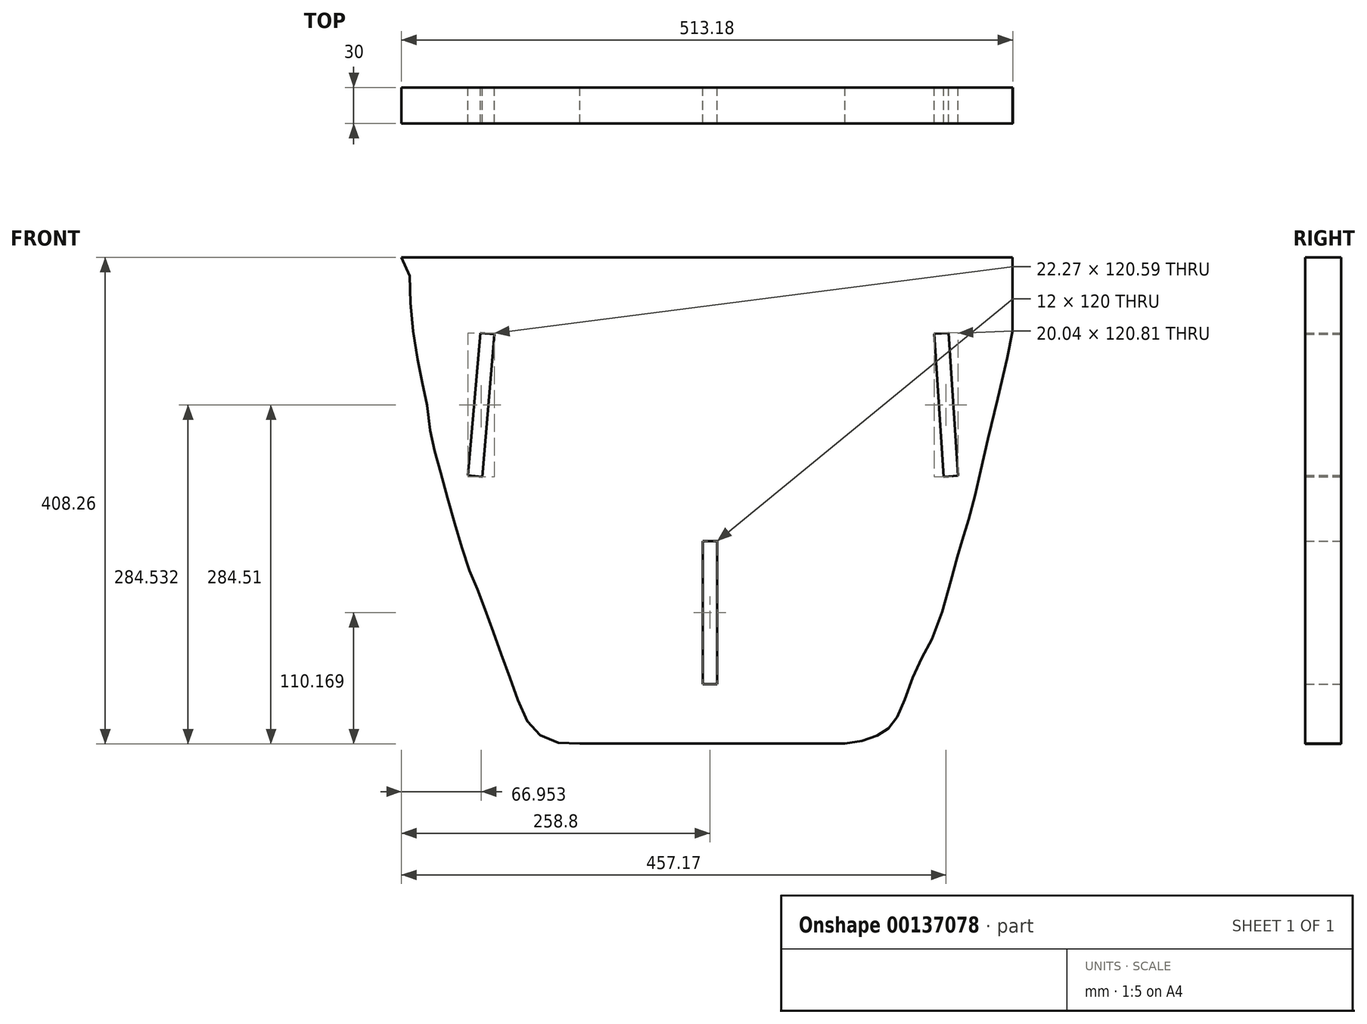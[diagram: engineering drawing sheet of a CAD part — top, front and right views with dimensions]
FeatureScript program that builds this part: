
annotation { "Feature Type Name" : "Feature", "Feature Type Description" : "" }
export const myFeature = defineFeature(function(context is Context, id is Id, definition is map)
    precondition{}
    {
        {
            var Q0;
            Q0=qCreatedBy(makeId("Front.planeOp"),FACE);
            var sketch = newSketch(context, id + "F0", { "sketchPlane" : qUnion([Q0])});
            skLineSegment(sketch, "E0", {"start": v(371.95, 251.63) * mm, "end": v(380.02, 131.63) * mm});
            skLineSegment(sketch, "E1", {"start": v(371.95, 251.63) * mm, "end": v(359.98, 250.83) * mm});
            skLineSegment(sketch, "E2", {"start": v(380.02, 131.63) * mm, "end": v(368.05, 130.83) * mm});
            skLineSegment(sketch, "E3", {"start": v(359.98, 250.83) * mm, "end": v(368.05, 130.83) * mm});
            skLineSegment(sketch, "E4", {"start": v(-21.04, 251.5) * mm, "end": v(-31.35, 131.95) * mm});
            skLineSegment(sketch, "E5", {"start": v(-21.04, 251.5) * mm, "end": v(-9.08, 250.47) * mm});
            skLineSegment(sketch, "E6", {"start": v(-31.35, 131.95) * mm, "end": v(-19.4, 130.92) * mm});
            skLineSegment(sketch, "E7", {"start": v(-9.08, 250.47) * mm, "end": v(-19.4, 130.92) * mm});
            skLineSegment(sketch, "E8", {"start": v(171.63, 76.87) * mm, "end": v(177.63, 76.87) * mm});
            skLineSegment(sketch, "E9", {"start": v(171.63, -43.13) * mm, "end": v(177.63, -43.13) * mm});
            skLineSegment(sketch, "E10", {"start": v(177.63, 76.87) * mm, "end": v(177.63, -43.13) * mm});
            skLineSegment(sketch, "E11", {"start": v(171.63, 76.87) * mm, "end": v(165.63, 76.87) * mm});
            skLineSegment(sketch, "E12", {"start": v(171.63, -43.13) * mm, "end": v(165.63, -43.13) * mm});
            skLineSegment(sketch, "E13", {"start": v(165.63, 76.87) * mm, "end": v(165.63, -43.13) * mm});
            skLineSegment(sketch, "E14", {"start": v(425.7, 314.96) * mm, "end": v(-87.17, 314.96) * mm});
            skLineSegment(sketch, "E15", {"start": v(285.12, -92.86) * mm, "end": v(62.42, -92.86) * mm});
            skFitSpline(sketch, "E16", {"points": [v(425.7, 314.96) * mm, v(425.7, 288.47) * mm, v(425.7, 261.81) * mm, v(425.7, 252.12) * mm, v(405.52, 163.66) * mm, v(393.4, 111.56) * mm, v(383.71, 77.63) * mm, v(377.65, 57.04) * mm, v(360.7, 0) * mm, v(346.15, -27.78) * mm, v(334.03, -59.29) * mm, v(325.55, -76.25) * mm, v(317.07, -83.52) * mm, v(303.74, -89.58) * mm, v(285.12, -92.86) * mm], "startDerivative": vector(2.08, -370.27) * mm, "endDerivative": vector(-337.13, -41.06) * mm});
            skFitSpline(sketch, "E17", {"points": [v(62.42, -92.86) * mm, v(46.86, -92.86) * mm, v(34.68, -88.7) * mm, v(24.08, -82.27) * mm, v(17, -71.67) * mm, v(9.61, -54.63) * mm, v(3.5, -37.28) * mm, v(-3.56, -17.67) * mm, v(-10, 0) * mm, v(-16.42, 18) * mm, v(-22.19, 32.86) * mm, v(-26.96, 45.57) * mm, v(-32.91, 59.08) * mm, v(-38.99, 80.78) * mm, v(-45.1, 99.77) * mm, v(-51.2, 123.52) * mm, v(-56.62, 142.51) * mm, v(-60.7, 157.44) * mm, v(-63.4, 172.36) * mm, v(-66.12, 193.4) * mm, v(-70.2, 211.03) * mm, v(-73.58, 228.67) * mm, v(-77.65, 255.13) * mm, v(-79.69, 281.58) * mm, v(-81.05, 303.3) * mm, v(-87.17, 314.96) * mm], "startDerivative": vector(-434.04, -31.01) * mm, "endDerivative": vector(-213.88, 307.85) * mm});
            skSolve(sketch);
        }
        {
            var Q0;
            Q0=makeQuery(id+"F0.imprint","IMPRINT",FACE,{"disambiguationData":[TD([[makeQuery(id+"F0.imprint","IMPRINT",EDGE,{"derivedFrom":sQuery(id+"F0.wireOp",EDGE,"E0")}),1.0]])]});
            var Q1;
            Q1=makeQuery(id+"F0.imprint","IMPRINT",FACE,{"disambiguationData":[TD([[makeQuery(id+"F0.imprint","IMPRINT",EDGE,{"derivedFrom":sQuery(id+"F0.wireOp",EDGE,"LRyQlrmy-n5ZQ-a9FJ-InVH-gw48jRSE0Qn0")}),1.0]])]});
            extrude(context, id + "F1", {"entities" : qUnion([Q0, Q1]), "depth" : 1 * mm});
        }
        {
            var Q0;
            Q0 = qSketchRegion(id + "F0", true);
            extrude(context, id + "F2", {"entities" : qUnion([Q0]), "operationType" : NewBodyOperationType.ADD, "depth" : 30 * mm});
        }
    });
